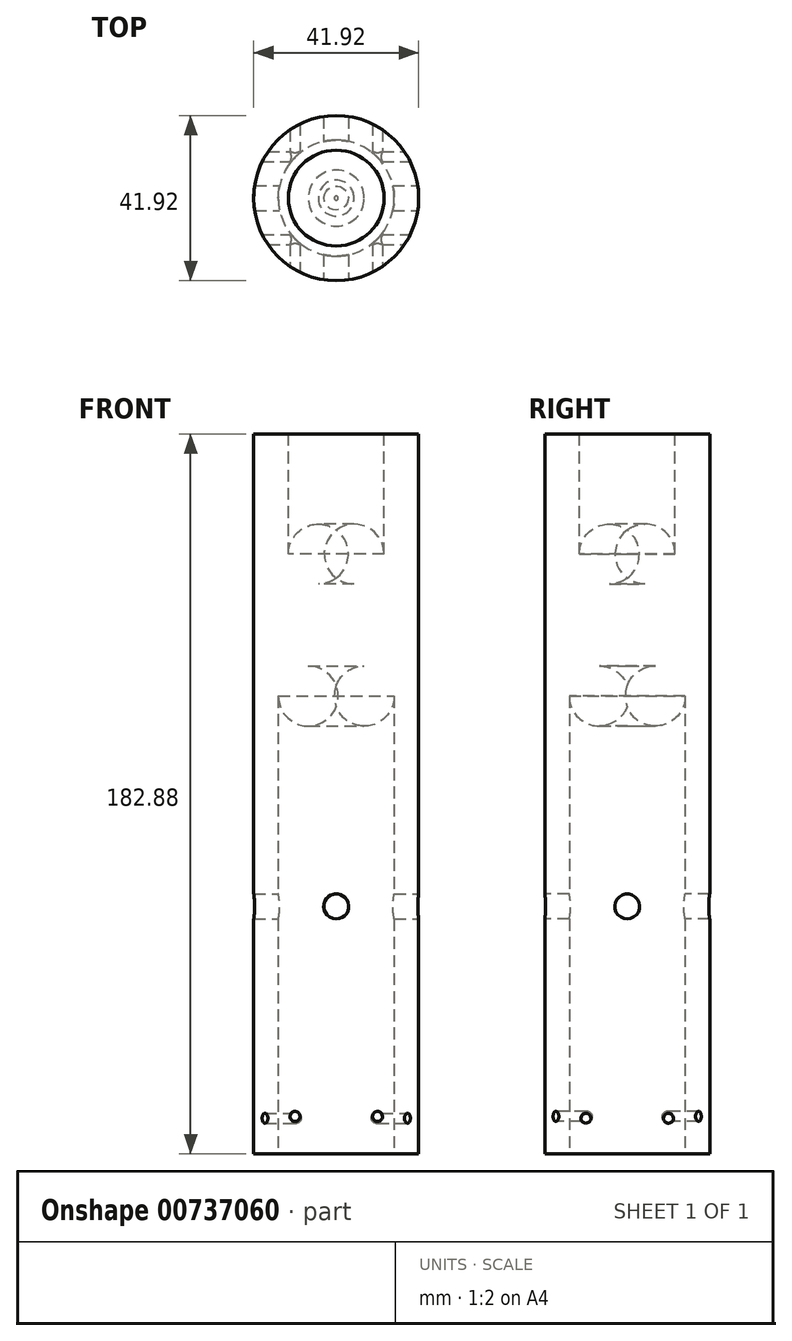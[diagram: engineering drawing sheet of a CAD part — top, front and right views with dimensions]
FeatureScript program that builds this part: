
annotation { "Feature Type Name" : "Feature", "Feature Type Description" : "" }
export const myFeature = defineFeature(function(context is Context, id is Id, definition is map)
    precondition{}
    {
        {
            var Q0;
            Q0=qCreatedBy(makeId("Front.planeOp"),FACE);
            var sketch = newSketch(context, id + "F0", { "sketchPlane" : qUnion([Q0])});
            skLineSegment(sketch, "E0", {"start": v(0, 0) * mm, "end": v(20.95, 0) * mm});
            skLineSegment(sketch, "E1", {"start": v(20.95, 0) * mm, "end": v(20.95, 182.88) * mm});
            skLineSegment(sketch, "E2", {"start": v(20.95, 182.88) * mm, "end": v(0, 182.88) * mm});
            skLineSegment(sketch, "E3", {"start": v(0, 182.88) * mm, "end": v(0, 0) * mm});
            skSolve(sketch);
        }
        {
            var Q0;
            Q0=qCreatedBy(makeId("Front.planeOp"),FACE);
            var sketch = newSketch(context, id + "F1", { "sketchPlane" : qUnion([Q0])});
            skLineSegment(sketch, "E4", {"start": v(0, -17.94) * mm, "end": v(0, 202.44) * mm});
            skSolve(sketch);
        }
        {
            var Q0;
            Q0=makeQuery(id+"F0.imprint","IMPRINT",FACE,{"disambiguationData":[TD([[makeQuery(id+"F0.imprint","IMPRINT",EDGE,{"derivedFrom":sQuery(id+"F0.wireOp",EDGE,"E0")}),1.0]])]});
            var Q1;
            Q1=sQuery(id+"F1.wireOp",EDGE,"E4");
            revolve(context, id + "F2", {"surfaceOperationType" : NewSurfaceOperationType.NEW, "entities" : qUnion([Q0]), "axis" : qUnion([Q1]), "revolveType" : RevolveType.FULL});
        }
        {
            var Q0;
            Q0=makeQuery(id+"F2.opRevolve","SWEPT_FACE",FACE,{"disambiguationData":[OSD([sQuery(id+"F0.wireOp",EDGE,"E0")])]});
            var sketch = newSketch(context, id + "F3", { "sketchPlane" : qUnion([Q0])});
            skCircle(sketch, "E5", {"center": v(0, 0) * mm, "radius": 14.73 * mm});
            skSolve(sketch);
        }
        {
            var Q0;
            Q0=makeQuery(id+"F3.imprint","IMPRINT",FACE,{"disambiguationData":[TD([[makeQuery(id+"F3.imprint","IMPRINT",EDGE,{"derivedFrom":sQuery(id+"F3.wireOp",EDGE,"E5")}),1.0]])]});
            var Q1;
            Q1=sQuery(id+"F3.wireOp",EDGE,"E5");
            extrude(context, id + "F4", {"entities" : qUnion([Q0]), "operationType" : NewBodyOperationType.REMOVE, "surfaceEntities" : qUnion([Q1]), "oppositeDirection" : true, "depth" : 123.95 * mm, "offsetDistance" : 25.4 * mm});
        }
        {
            var Q0;
            Q0=makeQuery(id+"F4.boolean.opBoolean","COPY",EDGE,{"derivedFrom":makeQuery(id+"F4.opExtrude","CAP_EDGE",EDGE,{"disambiguationData":[OSD([sQuery(id+"F3.wireOp",EDGE,"E5")])],"isStart":false})});
            fillet(context, id + "F5", {"entities" : qUnion([Q0]), "radius" : 7.62 * mm, "tangentPropagation" : true, "allowEdgeOverflow" : false});
        }
        {
            var Q0;
            Q0=makeQuery(id+"F2.opRevolve","SWEPT_FACE",FACE,{"disambiguationData":[OSD([sQuery(id+"F0.wireOp",EDGE,"E2")])]});
            var sketch = newSketch(context, id + "F6", { "sketchPlane" : qUnion([Q0])});
            skCircle(sketch, "E6", {"center": v(0, 0) * mm, "radius": 12.17 * mm});
            skSolve(sketch);
        }
        {
            var Q0;
            Q0=makeQuery(id+"F6.imprint","IMPRINT",FACE,{"disambiguationData":[TD([[makeQuery(id+"F6.imprint","IMPRINT",EDGE,{"derivedFrom":sQuery(id+"F6.wireOp",EDGE,"E6")}),1.0]])]});
            extrude(context, id + "F7", {"entities" : qUnion([Q0]), "operationType" : NewBodyOperationType.REMOVE, "oppositeDirection" : true, "depth" : 38.1 * mm, "offsetDistance" : 25.4 * mm});
        }
        {
            var Q0;
            Q0=makeQuery(id+"F7.boolean.opBoolean","COPY",EDGE,{"derivedFrom":makeQuery(id+"F7.opExtrude","CAP_EDGE",EDGE,{"disambiguationData":[OSD([sQuery(id+"F6.wireOp",EDGE,"E6")])],"isStart":false})});
            fillet(context, id + "F8", {"entities" : qUnion([Q0]), "radius" : 7.62 * mm, "tangentPropagation" : true, "allowEdgeOverflow" : false});
        }
        {
            var Q0;
            Q0=qCreatedBy(makeId("Front.planeOp"),FACE);
            cPlane(context, id + "F9", {"entities" : qUnion([Q0]), "cplaneType" : CPlaneType.OFFSET, "offset" : 25.4 * mm, "width" : 152.4 * mm, "height" : 152.4 * mm});
        }
        {
            var Q0;
            Q0=qCreatedBy(id+"F9.planeOp",FACE);
            var sketch = newSketch(context, id + "F10", { "sketchPlane" : qUnion([Q0])});
            skLineSegment(sketch, "E7", {"start": v(0, 0) * mm, "end": v(0, 62.87) * mm});
            skCircle(sketch, "E8", {"center": v(0, 62.87) * mm, "radius": 3.18 * mm});
            skSolve(sketch);
        }
        {
            var Q0;
            Q0=makeQuery(id+"F10.imprint","IMPRINT",FACE,{"disambiguationData":[TD([[makeQuery(id+"F10.imprint","IMPRINT",EDGE,{"derivedFrom":sQuery(id+"F10.wireOp",EDGE,"E8")}),1.0]])]});
            var Q1;
            Q1=sQuery(id+"F10.wireOp",EDGE,"E8");
            extrude(context, id + "F11", {"entities" : qUnion([Q0]), "operationType" : NewBodyOperationType.REMOVE, "surfaceEntities" : qUnion([Q1]), "oppositeDirection" : true, "depth" : 51.05 * mm, "offsetDistance" : 25.4 * mm});
        }
        {
            var Q0;
            Q0=qCreatedBy(makeId("Right.planeOp"),FACE);
            cPlane(context, id + "F12", {"entities" : qUnion([Q0]), "cplaneType" : CPlaneType.OFFSET, "offset" : 25.4 * mm, "width" : 152.4 * mm, "height" : 152.4 * mm});
        }
        {
            var Q0;
            Q0=qCreatedBy(id+"F12.planeOp",FACE);
            var sketch = newSketch(context, id + "F13", { "sketchPlane" : qUnion([Q0])});
            skLineSegment(sketch, "E9", {"start": v(0, 0) * mm, "end": v(0, 62.87) * mm});
            skCircle(sketch, "E10", {"center": v(0, 62.87) * mm, "radius": 3.18 * mm});
            skLineSegment(sketch, "E11", {"start": v(0, 0) * mm, "end": v(0, 9.07) * mm});
            skLineSegment(sketch, "E12", {"start": v(0, 9.07) * mm, "end": v(10.48, 9.07) * mm});
            skLineSegment(sketch, "E13", {"start": v(0, 9.07) * mm, "end": v(-10.5, 9.07) * mm});
            skCircle(sketch, "E14", {"center": v(-10.5, 9.07) * mm, "radius": 1.27 * mm});
            skCircle(sketch, "E15", {"center": v(10.48, 9.07) * mm, "radius": 1.27 * mm});
            skSolve(sketch);
        }
        {
            var Q0;
            Q0 = qSketchRegion(id + "F13", true);
            extrude(context, id + "F14", {"entities" : qUnion([Q0]), "operationType" : NewBodyOperationType.REMOVE, "oppositeDirection" : true, "depth" : 50.8 * mm, "offsetDistance" : 25.4 * mm});
        }
        {
            var Q0;
            Q0=qCreatedBy(id+"F9.planeOp",FACE);
            var sketch = newSketch(context, id + "F15", { "sketchPlane" : qUnion([Q0])});
            skLineSegment(sketch, "E16", {"start": v(0, 0) * mm, "end": v(0, 9.53) * mm});
            skLineSegment(sketch, "E17", {"start": v(0, 9.53) * mm, "end": v(10.48, 9.53) * mm});
            skLineSegment(sketch, "E18", {"start": v(0, 9.53) * mm, "end": v(-10.48, 9.53) * mm});
            skCircle(sketch, "E19", {"center": v(10.48, 9.53) * mm, "radius": 1.27 * mm});
            skCircle(sketch, "E20", {"center": v(-10.48, 9.53) * mm, "radius": 1.27 * mm});
            skSolve(sketch);
        }
        {
            var Q0;
            Q0=makeQuery(id+"F15.imprint","IMPRINT",FACE,{"disambiguationData":[TD([[makeQuery(id+"F15.imprint","IMPRINT",EDGE,{"derivedFrom":sQuery(id+"F15.wireOp",EDGE,"E20")}),1.0]])]});
            var Q1;
            Q1=makeQuery(id+"F15.imprint","IMPRINT",FACE,{"disambiguationData":[TD([[makeQuery(id+"F15.imprint","IMPRINT",EDGE,{"derivedFrom":sQuery(id+"F15.wireOp",EDGE,"E19")}),1.0]])]});
            extrude(context, id + "F16", {"entities" : qUnion([Q0, Q1]), "operationType" : NewBodyOperationType.REMOVE, "oppositeDirection" : true, "depth" : 50.8 * mm, "offsetDistance" : 25.4 * mm});
        }
    });
